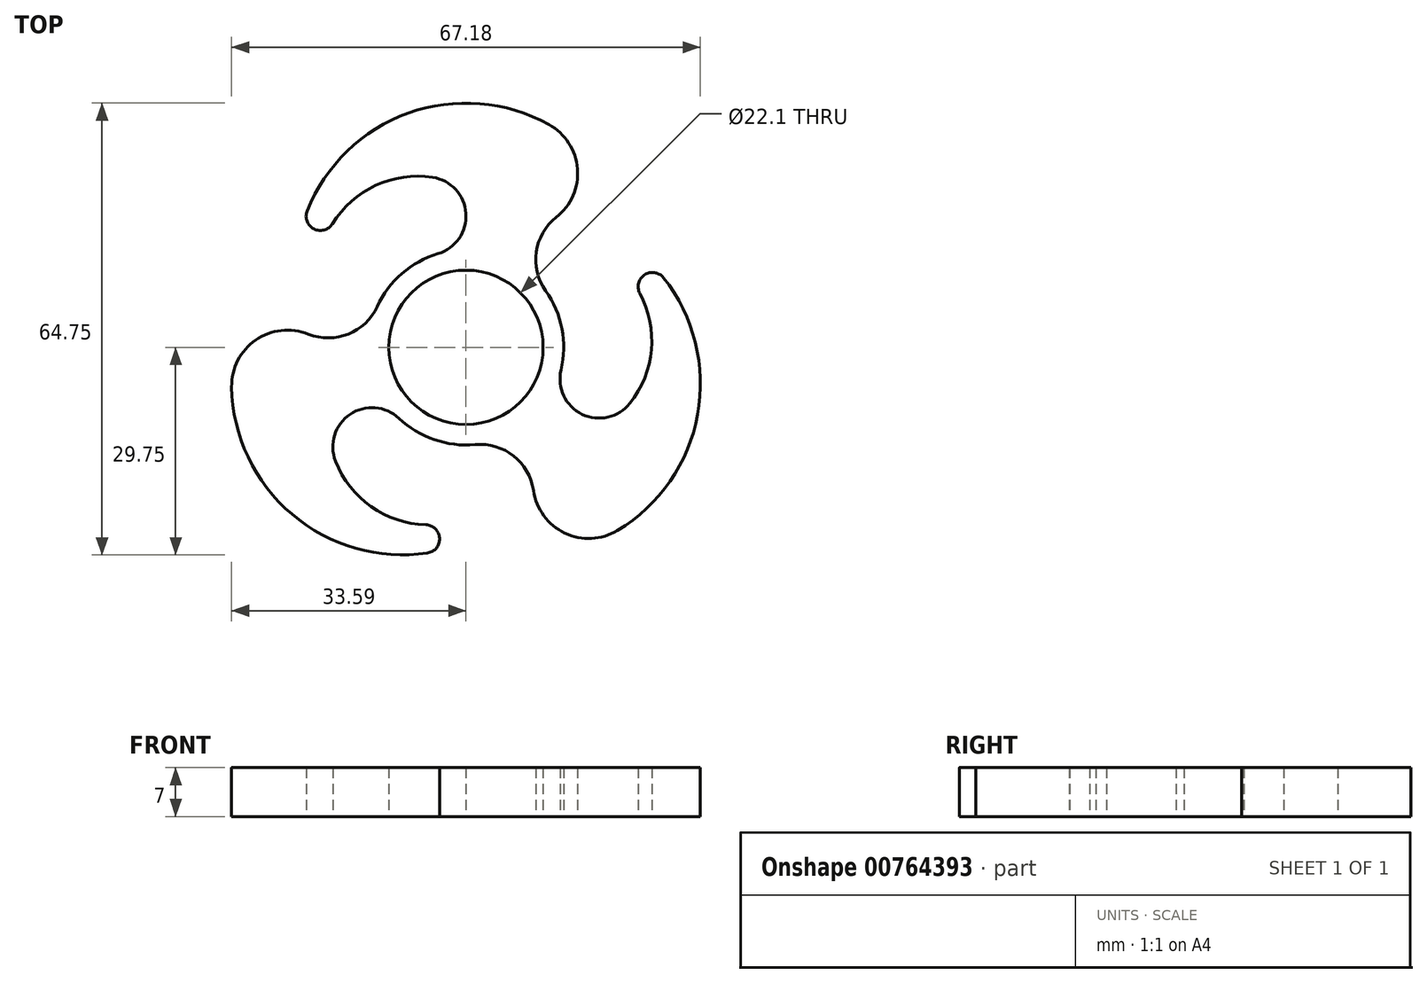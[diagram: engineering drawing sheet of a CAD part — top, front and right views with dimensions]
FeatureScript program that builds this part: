
annotation { "Feature Type Name" : "Feature", "Feature Type Description" : "" }
export const myFeature = defineFeature(function(context is Context, id is Id, definition is map)
    precondition{}
    {
        {
            var Q0;
            Q0=qCreatedBy(makeId("Top.planeOp"),FACE);
            var sketch = newSketch(context, id + "F0", { "sketchPlane" : qUnion([Q0])});
            skCircle(sketch, "E0", {"center": v(0, 0) * mm, "radius": 11.05 * mm});
            skCircle(sketch, "E1", {"center": v(0, 0) * mm, "radius": 35 * mm, "construction": true});
            skCircle(sketch, "E2", {"center": v(0, 0) * mm, "radius": 14 * mm});
            skArc(sketch, "E3", {"start": v(11.88, 31.93) * mm, "mid": v(-8.25, 33.57) * mm, "end": v(-22.78, 19.53) * mm});
            skArc(sketch, "E4", {"start": v(12.95, 18.65) * mm, "mid": v(15.97, 25.57) * mm, "end": v(11.88, 31.93) * mm});
            skArc(sketch, "E5", {"start": v(12.95, 18.65) * mm, "mid": v(10.08, 13.67) * mm, "end": v(11.42, 8.1) * mm});
            skArc(sketch, "E6", {"start": v(-4.01, 13.41) * mm, "mid": v(-0.01, 19.2) * mm, "end": v(-4.78, 24.36) * mm});
            skArc(sketch, "E7", {"start": v(-22.78, 19.53) * mm, "mid": v(-21.8, 16.96) * mm, "end": v(-19.15, 17.7) * mm});
            skArc(sketch, "E8.trimOffspring", {"start": v(-4.78, 24.36) * mm, "mid": v(-12.97, 23.19) * mm, "end": v(-19.15, 17.7) * mm});
            skPoint(sketch, "E9.center", {"position": v(0, -0.87) * mm});
            skArc(sketch, "E10.1.0", {"start": v(-5.53, -29.49) * mm, "mid": v(-3.8, -27.36) * mm, "end": v(-5.76, -25.44) * mm});
            skArc(sketch, "E10.1.1", {"start": v(-33.59, -5.68) * mm, "mid": v(-24.94, -23.93) * mm, "end": v(-5.53, -29.49) * mm});
            skArc(sketch, "E10.1.2", {"start": v(-22.62, 1.9) * mm, "mid": v(-30.13, 1.05) * mm, "end": v(-33.59, -5.68) * mm});
            skArc(sketch, "E10.1.3", {"start": v(-22.62, 1.9) * mm, "mid": v(-16.88, 1.9) * mm, "end": v(-12.72, 5.85) * mm});
            skArc(sketch, "E10.1.4", {"start": v(-9.61, -10.18) * mm, "mid": v(-16.62, -9.6) * mm, "end": v(-18.7, -16.32) * mm});
            skArc(sketch, "E10.1.5", {"start": v(-18.7, -16.32) * mm, "mid": v(-13.6, -22.82) * mm, "end": v(-5.76, -25.44) * mm});
            skArc(sketch, "E10.2.0", {"start": v(28.3, 9.96) * mm, "mid": v(25.59, 10.4) * mm, "end": v(24.91, 7.73) * mm});
            skArc(sketch, "E10.2.1", {"start": v(21.71, -26.25) * mm, "mid": v(33.2, -9.64) * mm, "end": v(28.3, 9.96) * mm});
            skArc(sketch, "E10.2.2", {"start": v(9.67, -20.54) * mm, "mid": v(14.16, -26.62) * mm, "end": v(21.71, -26.25) * mm});
            skArc(sketch, "E10.2.3", {"start": v(9.67, -20.54) * mm, "mid": v(6.8, -15.57) * mm, "end": v(1.3, -13.94) * mm});
            skArc(sketch, "E10.2.4", {"start": v(13.62, -3.23) * mm, "mid": v(16.63, -9.58) * mm, "end": v(23.48, -8.04) * mm});
            skArc(sketch, "E10.2.5", {"start": v(23.48, -8.04) * mm, "mid": v(26.57, -0.37) * mm, "end": v(24.91, 7.73) * mm});
            skSolve(sketch);
        }
        {
            var Q0;
            {var subQ1=sQuery(id+"F0.wireOp",EDGE,"E3");Q0=makeQuery(id+"F0.imprint","IMPRINT",FACE,{"disambiguationData":[TD([[makeQuery(id+"F0.imprint","IMPRINT",EDGE,{"derivedFrom":subQ1}),1.0]])]});}
            var Q1;
            Q1=makeQuery(id+"F0.imprint","IMPRINT",FACE,{"disambiguationData":[TD([[makeQuery(id+"F0.imprint","IMPRINT",EDGE,{"derivedFrom":sQuery(id+"F0.wireOp",EDGE,"E9.1.0")}),1.0]])]});
            var Q2;
            Q2=makeQuery(id+"F0.imprint","IMPRINT",FACE,{"disambiguationData":[TD([[makeQuery(id+"F0.imprint","IMPRINT",EDGE,{"derivedFrom":sQuery(id+"F0.wireOp",EDGE,"E0")}),-1.0]])]});
            var Q3;
            Q3=makeQuery(id+"F0.imprint","IMPRINT",FACE,{"disambiguationData":[TD([[makeQuery(id+"F0.imprint","IMPRINT",EDGE,{"derivedFrom":sQuery(id+"F0.wireOp",EDGE,"E9.2.0")}),1.0]])]});
            var Q4;
            Q4=makeQuery(id+"F0.imprint","IMPRINT",FACE,{"disambiguationData":[TD([[makeQuery(id+"F0.imprint","IMPRINT",EDGE,{"derivedFrom":sQuery(id+"F0.wireOp",EDGE,"E9.3.0")}),1.0]])]});
            var Q5;
            Q5=makeQuery(id+"F0.imprint","IMPRINT",FACE,{"disambiguationData":[TD([[makeQuery(id+"F0.imprint","IMPRINT",EDGE,{"derivedFrom":sQuery(id+"F0.wireOp",EDGE,"E10.1.0")}),1.0]])]});
            var Q6;
            Q6=makeQuery(id+"F0.imprint","IMPRINT",FACE,{"disambiguationData":[TD([[makeQuery(id+"F0.imprint","IMPRINT",EDGE,{"derivedFrom":sQuery(id+"F0.wireOp",EDGE,"E10.2.0")}),1.0]])]});
            extrude(context, id + "F1", {"entities" : qUnion([Q0, Q1, Q2, Q3, Q4, Q5, Q6]), "depth" : 7 * mm, "offsetDistance" : 25 * mm});
        }
    });
